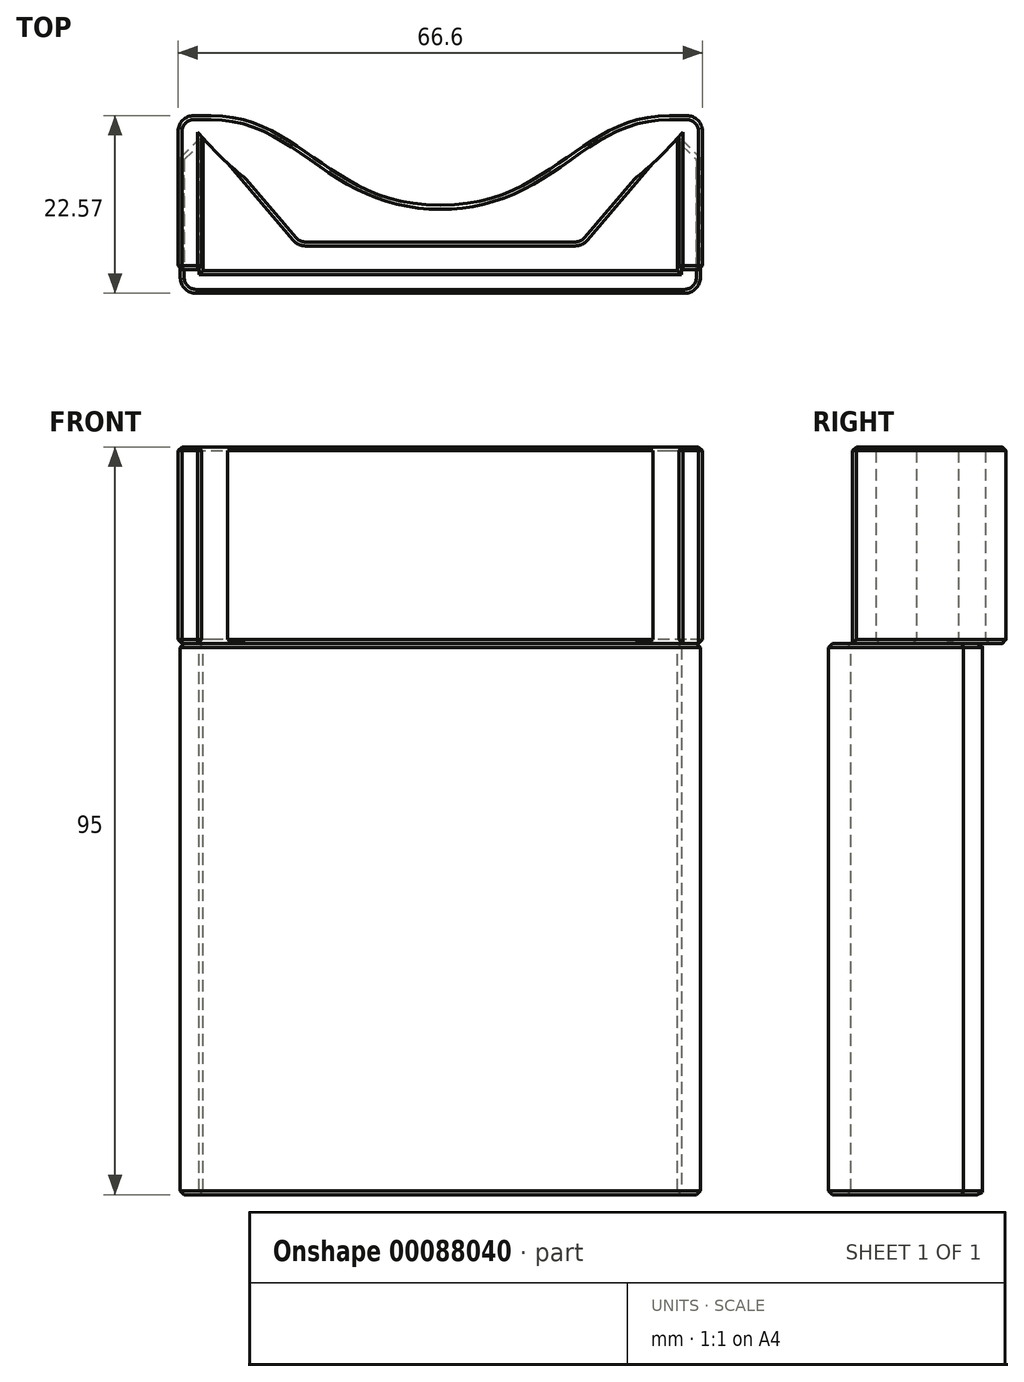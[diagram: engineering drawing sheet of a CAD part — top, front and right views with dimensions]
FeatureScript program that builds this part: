
annotation { "Feature Type Name" : "Feature", "Feature Type Description" : "" }
export const myFeature = defineFeature(function(context is Context, id is Id, definition is map)
    precondition{}
    {
        {
            var Q0;
            Q0=qCreatedBy(makeId("Top.planeOp"),FACE);
            var sketch = newSketch(context, id + "F0", { "sketchPlane" : qUnion([Q0])});
            skLineSegment(sketch, "E0", {"start": v(0, 0) * mm, "end": v(30, 0) * mm, "construction": true});
            skLineSegment(sketch, "E1", {"start": v(30, 0) * mm, "end": v(30, 40) * mm, "construction": true});
            skLineSegment(sketch, "E2", {"start": v(30, 40) * mm, "end": v(27, 40) * mm, "construction": true});
            skLineSegment(sketch, "E3", {"start": v(27, 40) * mm, "end": v(27, 3) * mm, "construction": true});
            skLineSegment(sketch, "E4", {"start": v(27, 3) * mm, "end": v(0, 3) * mm, "construction": true});
            skLineSegment(sketch, "E5", {"start": v(0, 3) * mm, "end": v(0, 0) * mm, "construction": true});
            skLineSegment(sketch, "E6.MirrorCS", {"start": v(-27, 3) * mm, "end": v(0, 3) * mm, "construction": true});
            skLineSegment(sketch, "E7.MirrorCS", {"start": v(0, 0) * mm, "end": v(-30, 0) * mm, "construction": true});
            skLineSegment(sketch, "E8.MirrorCS", {"start": v(-30, 0) * mm, "end": v(-30, 40) * mm, "construction": true});
            skLineSegment(sketch, "E9.MirrorCS", {"start": v(-27, 40) * mm, "end": v(-27, 3) * mm, "construction": true});
            skLineSegment(sketch, "E10.MirrorCS", {"start": v(-30, 40) * mm, "end": v(-27, 40) * mm, "construction": true});
            skArc(sketch, "E11", {"start": v(-30, 16.54) * mm, "mid": v(-28.54, 14.97) * mm, "end": v(-27, 13.49) * mm});
            skArc(sketch, "E12", {"start": v(-27, 13.49) * mm, "mid": v(0, 3) * mm, "end": v(27, 13.49) * mm, "construction": true});
            skArc(sketch, "E13", {"start": v(27, 13.49) * mm, "mid": v(28.54, 14.97) * mm, "end": v(30, 16.54) * mm});
            skArc(sketch, "E14", {"start": v(30, 16.54) * mm, "mid": v(0, 83) * mm, "end": v(-30, 16.54) * mm, "construction": true});
            skLineSegment(sketch, "E15", {"start": v(-27, 13.49) * mm, "end": v(-18.68, 3.7) * mm});
            skLineSegment(sketch, "E16", {"start": v(-17.15, 3) * mm, "end": v(0, 3) * mm});
            skLineSegment(sketch, "E17", {"start": v(-30.3, 16.54) * mm, "end": v(-30.3, 0) * mm});
            skLineSegment(sketch, "E18", {"start": v(-30.3, 0) * mm, "end": v(-33.3, 0) * mm});
            skLineSegment(sketch, "E19", {"start": v(-33.3, 0) * mm, "end": v(-33.3, 17.54) * mm});
            skLineSegment(sketch, "E20", {"start": v(-31.3, 19.54) * mm, "end": v(-29.14, 19.54) * mm});
            skLineSegment(sketch, "E21", {"start": v(0, 6) * mm, "end": v(0, 3) * mm, "construction": true});
            skLineSegment(sketch, "E22.MirrorCS", {"start": v(17.15, 3) * mm, "end": v(0, 3) * mm});
            skLineSegment(sketch, "E23.MirrorCS", {"start": v(27, 13.49) * mm, "end": v(18.68, 3.7) * mm});
            skLineSegment(sketch, "E24.MirrorCS", {"start": v(31.3, 19.54) * mm, "end": v(29.14, 19.54) * mm});
            skLineSegment(sketch, "E25.MirrorCS", {"start": v(30.3, 16.54) * mm, "end": v(30.3, 0) * mm});
            skLineSegment(sketch, "E26.MirrorCS", {"start": v(33.3, 0) * mm, "end": v(33.3, 17.54) * mm});
            skLineSegment(sketch, "E27.MirrorCS", {"start": v(30.3, 0) * mm, "end": v(33.3, 0) * mm});
            skPoint(sketch, "E28.visualSharp", {"position": v(-33.3, 19.54) * mm});
            skArc(sketch, "E28.filletArc", {"start": v(-31.3, 19.54) * mm, "mid": v(-32.71, 18.96) * mm, "end": v(-33.3, 17.54) * mm});
            skPoint(sketch, "E29.visualSharp", {"position": v(-16.7, 6) * mm});
            skPoint(sketch, "E30.visualSharp", {"position": v(-18.08, 3) * mm});
            skArc(sketch, "E30.filletArc", {"start": v(-18.68, 3.7) * mm, "mid": v(-18, 3.18) * mm, "end": v(-17.15, 3) * mm});
            skPoint(sketch, "E31.visualSharp", {"position": v(18.08, 3) * mm});
            skArc(sketch, "E31.filletArc", {"start": v(17.15, 3) * mm, "mid": v(18, 3.18) * mm, "end": v(18.68, 3.7) * mm});
            skPoint(sketch, "E32.visualSharp", {"position": v(16.7, 6) * mm});
            skArc(sketch, "E32.filletArc", {"start": v(15.77, 6) * mm, "mid": v(16.6, 6.18) * mm, "end": v(17.29, 6.7) * mm});
            skPoint(sketch, "E33.visualSharp", {"position": v(28.21, 19.54) * mm});
            skPoint(sketch, "E34.visualSharp", {"position": v(33.3, 19.54) * mm});
            skArc(sketch, "E34.filletArc", {"start": v(33.3, 17.54) * mm, "mid": v(32.71, 18.96) * mm, "end": v(31.3, 19.54) * mm});
            skLineSegment(sketch, "E35", {"start": v(-30.3, 16.54) * mm, "end": v(-30.3, 16.89) * mm});
            skLineSegment(sketch, "E36", {"start": v(-30.3, 16.89) * mm, "end": v(-30, 16.54) * mm});
            skLineSegment(sketch, "E37", {"start": v(30.3, 16.54) * mm, "end": v(30.3, 16.89) * mm});
            skLineSegment(sketch, "E38", {"start": v(30.3, 16.89) * mm, "end": v(30, 16.54) * mm});
            skFitSpline(sketch, "E39", {"points": [v(-29.14, 19.54) * mm, v(0, 8.16) * mm], "startDerivative": vector(34.38, 0) * mm, "endDerivative": vector(42.32, 0) * mm});
            skFitSpline(sketch, "E40.MirrorCS", {"points": [v(29.14, 19.54) * mm, v(0, 8.16) * mm], "startDerivative": vector(-34.38, 0) * mm, "endDerivative": vector(-42.32, 0) * mm});
            skSolve(sketch);
        }
        {
            var Q0;
            Q0 = qSketchRegion(id + "F0", true);
            extrude(context, id + "F1", {"entities" : qUnion([Q0]), "depth" : 25 * mm});
        }
        {
            var Q0;
            Q0=makeQuery(id+"F1.opExtrude","CAP_EDGE",EDGE,{"disambiguationData":[OSD([sQuery(id+"F0.wireOp",EDGE,"E23.MirrorCS")])],"isStart":true});
            var Q1;
            Q1=makeQuery(id+"F1.opExtrude","CAP_EDGE",EDGE,{"disambiguationData":[OSD([sQuery(id+"F0.wireOp",EDGE,"E25.MirrorCS"),sQuery(id+"F0.wireOp",EDGE,"E37")])],"isStart":true});
            var Q2;
            Q2=makeQuery(id+"F1.opExtrude","CAP_EDGE",EDGE,{"disambiguationData":[OSD([sQuery(id+"F0.wireOp",EDGE,"E26.MirrorCS")])],"isStart":true});
            var Q3;
            Q3=makeQuery(id+"F1.opExtrude","CAP_EDGE",EDGE,{"disambiguationData":[OSD([sQuery(id+"F0.wireOp",EDGE,"E26.MirrorCS")])],"isStart":false});
            var Q4;
            Q4=makeQuery(id+"F1.opExtrude","CAP_EDGE",EDGE,{"disambiguationData":[OSD([sQuery(id+"F0.wireOp",EDGE,"E16"),sQuery(id+"F0.wireOp",EDGE,"E22.MirrorCS")])],"isStart":false});
            var Q5;
            Q5=makeQuery(id+"F1.opExtrude","CAP_EDGE",EDGE,{"disambiguationData":[OSD([sQuery(id+"F0.wireOp",EDGE,"E25.MirrorCS"),sQuery(id+"F0.wireOp",EDGE,"E37")])],"isStart":false});
            var Q6;
            Q6=makeQuery(id+"F1.opExtrude","CAP_EDGE",EDGE,{"disambiguationData":[OSD([sQuery(id+"F0.wireOp",EDGE,"E27.MirrorCS")])],"isStart":false});
            var Q7;
            Q7=makeQuery(id+"F1.opExtrude","CAP_EDGE",EDGE,{"disambiguationData":[OSD([sQuery(id+"F0.wireOp",EDGE,"E18")])],"isStart":false});
            var Q8;
            Q8=makeQuery(id+"F1.opExtrude","CAP_EDGE",EDGE,{"disambiguationData":[OSD([sQuery(id+"F0.wireOp",EDGE,"E17"),sQuery(id+"F0.wireOp",EDGE,"E35")])],"isStart":false});
            var Q9;
            Q9=makeQuery(id+"F1.opExtrude","SWEPT_EDGE",EDGE,{"disambiguationData":[OSD([sQuery(id+"F0.wireOp",EDGE,"E18"),sQuery(id+"F0.wireOp",EDGE,"E19")])]});
            var Q10;
            Q10=makeQuery(id+"F1.opExtrude","SWEPT_EDGE",EDGE,{"disambiguationData":[OSD([sQuery(id+"F0.wireOp",EDGE,"E25.MirrorCS"),sQuery(id+"F0.wireOp",EDGE,"E27.MirrorCS")])]});
            var Q11;
            Q11=makeQuery(id+"F1.opExtrude","SWEPT_EDGE",EDGE,{"disambiguationData":[OSD([sQuery(id+"F0.wireOp",EDGE,"E26.MirrorCS"),sQuery(id+"F0.wireOp",EDGE,"E27.MirrorCS")])]});
            var Q12;
            Q12=makeQuery(id+"F1.opExtrude","SWEPT_EDGE",EDGE,{"disambiguationData":[OSD([sQuery(id+"F0.wireOp",EDGE,"E17"),sQuery(id+"F0.wireOp",EDGE,"E18")])]});
            var Q13;
            Q13=makeQuery(id+"F1.opExtrude","CAP_EDGE",EDGE,{"disambiguationData":[OSD([sQuery(id+"F0.wireOp",EDGE,"E18")])],"isStart":true});
            var Q14;
            Q14=makeQuery(id+"F1.opExtrude","CAP_EDGE",EDGE,{"disambiguationData":[OSD([sQuery(id+"F0.wireOp",EDGE,"E17"),sQuery(id+"F0.wireOp",EDGE,"E35")])],"isStart":true});
            chamfer(context, id + "F2", {"entities" : qUnion([Q0, Q1, Q2, Q3, Q4, Q5, Q6, Q7, Q8, Q9, Q10, Q11, Q12, Q13, Q14]), "width" : 0.5 * mm, "tangentPropagation" : true});
        }
        {
            var Q0;
            Q0=qCreatedBy(makeId("Top.planeOp"),FACE);
            var sketch = newSketch(context, id + "F3", { "sketchPlane" : qUnion([Q0])});
            skPoint(sketch, "E41.0", {"position": v(-30, 16.54) * mm});
            skLineSegment(sketch, "E41.1", {"start": v(0, 0) * mm, "end": v(-30, 0) * mm, "construction": true});
            skLineSegment(sketch, "E41.2", {"start": v(0, 3) * mm, "end": v(0, 0) * mm, "construction": true});
            skLineSegment(sketch, "E42", {"start": v(-30, 0) * mm, "end": v(-30, 16.54) * mm, "construction": true});
            skLineSegment(sketch, "E43", {"start": v(-30.15, 16.54) * mm, "end": v(-30.15, -0.15) * mm});
            skLineSegment(sketch, "E44", {"start": v(-30.15, -0.15) * mm, "end": v(0, -0.15) * mm});
            skLineSegment(sketch, "E45", {"start": v(-30.15, 16.54) * mm, "end": v(-33.03, 16.54) * mm});
            skLineSegment(sketch, "E46", {"start": v(-33.03, 16.54) * mm, "end": v(-33.03, -3.03) * mm});
            skLineSegment(sketch, "E47", {"start": v(-33.03, -3.03) * mm, "end": v(0, -3.03) * mm});
            skLineSegment(sketch, "E48.MirrorCS", {"start": v(30.15, -0.15) * mm, "end": v(0, -0.15) * mm});
            skLineSegment(sketch, "E49.MirrorCS", {"start": v(33.03, -3.03) * mm, "end": v(0, -3.03) * mm});
            skLineSegment(sketch, "E50.MirrorCS", {"start": v(30.15, 16.54) * mm, "end": v(30.15, -0.15) * mm});
            skLineSegment(sketch, "E51.MirrorCS", {"start": v(33.03, 16.54) * mm, "end": v(33.03, -3.03) * mm});
            skLineSegment(sketch, "E52.MirrorCS", {"start": v(30.15, 16.54) * mm, "end": v(33.03, 16.54) * mm});
            skLineSegment(sketch, "E53", {"start": v(-30.15, -0.15) * mm, "end": v(-30.15, -3.03) * mm, "construction": true});
            skSolve(sketch);
        }
        {
            var Q0;
            Q0=makeQuery(id+"F3.imprint","IMPRINT",FACE,{"disambiguationData":[TD([[makeQuery(id+"F3.imprint","IMPRINT",EDGE,{"derivedFrom":sQuery(id+"F3.wireOp",EDGE,"E43")}),-1.0]])]});
            extrude(context, id + "F4", {"entities" : qUnion([Q0]), "oppositeDirection" : true, "depth" : 70 * mm});
        }
        {
            var Q0;
            Q0=makeQuery(id+"F4.opExtrude","SWEPT_EDGE",EDGE,{"disambiguationData":[OSD([sQuery(id+"F3.wireOp",EDGE,"E45"),sQuery(id+"F3.wireOp",EDGE,"E46")])]});
            var Q1;
            Q1=makeQuery(id+"F4.opExtrude","SWEPT_EDGE",EDGE,{"disambiguationData":[OSD([sQuery(id+"F3.wireOp",EDGE,"E51.MirrorCS"),sQuery(id+"F3.wireOp",EDGE,"E52.MirrorCS")])]});
            chamfer(context, id + "F5", {"entities" : qUnion([Q0, Q1]), "width" : (5 * 0.48) * mm, "tangentPropagation" : true});
        }
        {
            var Q0;
            Q0=makeQuery(id+"F4.opExtrude","SWEPT_EDGE",EDGE,{"disambiguationData":[OSD([sQuery(id+"F3.wireOp",EDGE,"E46"),sQuery(id+"F3.wireOp",EDGE,"E47")])]});
            var Q1;
            Q1=makeQuery(id+"F4.opExtrude","SWEPT_EDGE",EDGE,{"disambiguationData":[OSD([sQuery(id+"F3.wireOp",EDGE,"E49.MirrorCS"),sQuery(id+"F3.wireOp",EDGE,"E51.MirrorCS")])]});
            fillet(context, id + "F6", {"entities" : qUnion([Q0, Q1]), "radius" : 2 * mm, "tangentPropagation" : true, "allowEdgeOverflow" : false});
        }
        {
            var Q0;
            Q0=makeQuery(id+"F4.opExtrude","CAP_EDGE",EDGE,{"disambiguationData":[OSD([sQuery(id+"F3.wireOp",EDGE,"E46")])],"isStart":true});
            var Q1;
            {var subQ0=sQuery(id+"F3.wireOp",EDGE,"E46");var subQ1=sQuery(id+"F3.wireOp",EDGE,"E45");Q1=makeQuery(id+"F5.opChamfer","BLEND_EDGE",EDGE,{"blendedFrom":[makeQuery(id+"F4.opExtrude","SWEPT_EDGE",EDGE,{"disambiguationData":[OSD([subQ1,subQ0])]}),makeQuery(id+"F4.opExtrude","CAP_FACE",FACE,{"disambiguationData":[OSD([sQuery(id+"F3.wireOp",EDGE,"E43"),sQuery(id+"F3.wireOp",EDGE,"E44"),subQ1,subQ0,sQuery(id+"F3.wireOp",EDGE,"E47"),sQuery(id+"F3.wireOp",EDGE,"E48.MirrorCS"),sQuery(id+"F3.wireOp",EDGE,"E49.MirrorCS"),sQuery(id+"F3.wireOp",EDGE,"E50.MirrorCS"),sQuery(id+"F3.wireOp",EDGE,"E51.MirrorCS"),sQuery(id+"F3.wireOp",EDGE,"E52.MirrorCS")])],"isStart":true})],"blendedInto":[makeQuery(id+"F4.opExtrude","CAP_FACE",FACE,{"disambiguationData":[OSD([sQuery(id+"F3.wireOp",EDGE,"E43"),sQuery(id+"F3.wireOp",EDGE,"E44"),subQ1,subQ0,sQuery(id+"F3.wireOp",EDGE,"E47"),sQuery(id+"F3.wireOp",EDGE,"E48.MirrorCS"),sQuery(id+"F3.wireOp",EDGE,"E49.MirrorCS"),sQuery(id+"F3.wireOp",EDGE,"E50.MirrorCS"),sQuery(id+"F3.wireOp",EDGE,"E51.MirrorCS"),sQuery(id+"F3.wireOp",EDGE,"E52.MirrorCS")])],"isStart":true})]});}
            var Q2;
            Q2=makeQuery(id+"F4.opExtrude","CAP_EDGE",EDGE,{"disambiguationData":[OSD([sQuery(id+"F3.wireOp",EDGE,"E43")])],"isStart":true});
            var Q3;
            Q3=makeQuery(id+"F4.opExtrude","CAP_EDGE",EDGE,{"disambiguationData":[OSD([sQuery(id+"F3.wireOp",EDGE,"E44"),sQuery(id+"F3.wireOp",EDGE,"E48.MirrorCS")])],"isStart":true});
            var Q4;
            Q4=makeQuery(id+"F4.opExtrude","CAP_EDGE",EDGE,{"disambiguationData":[OSD([sQuery(id+"F3.wireOp",EDGE,"E50.MirrorCS")])],"isStart":true});
            var Q5;
            {var subQ0=sQuery(id+"F3.wireOp",EDGE,"E52.MirrorCS");var subQ1=sQuery(id+"F3.wireOp",EDGE,"E51.MirrorCS");Q5=makeQuery(id+"F5.opChamfer","BLEND_EDGE",EDGE,{"blendedFrom":[makeQuery(id+"F4.opExtrude","SWEPT_EDGE",EDGE,{"disambiguationData":[OSD([subQ1,subQ0])]}),makeQuery(id+"F4.opExtrude","CAP_FACE",FACE,{"disambiguationData":[OSD([sQuery(id+"F3.wireOp",EDGE,"E43"),sQuery(id+"F3.wireOp",EDGE,"E44"),sQuery(id+"F3.wireOp",EDGE,"E45"),sQuery(id+"F3.wireOp",EDGE,"E46"),sQuery(id+"F3.wireOp",EDGE,"E47"),sQuery(id+"F3.wireOp",EDGE,"E48.MirrorCS"),sQuery(id+"F3.wireOp",EDGE,"E49.MirrorCS"),sQuery(id+"F3.wireOp",EDGE,"E50.MirrorCS"),subQ1,subQ0])],"isStart":true})],"blendedInto":[makeQuery(id+"F4.opExtrude","CAP_FACE",FACE,{"disambiguationData":[OSD([sQuery(id+"F3.wireOp",EDGE,"E43"),sQuery(id+"F3.wireOp",EDGE,"E44"),sQuery(id+"F3.wireOp",EDGE,"E45"),sQuery(id+"F3.wireOp",EDGE,"E46"),sQuery(id+"F3.wireOp",EDGE,"E47"),sQuery(id+"F3.wireOp",EDGE,"E48.MirrorCS"),sQuery(id+"F3.wireOp",EDGE,"E49.MirrorCS"),sQuery(id+"F3.wireOp",EDGE,"E50.MirrorCS"),subQ1,subQ0])],"isStart":true})]});}
            var Q6;
            Q6=makeQuery(id+"F4.opExtrude","CAP_EDGE",EDGE,{"disambiguationData":[OSD([sQuery(id+"F3.wireOp",EDGE,"E46")])],"isStart":false});
            var Q7;
            Q7=makeQuery(id+"F4.opExtrude","CAP_EDGE",EDGE,{"disambiguationData":[OSD([sQuery(id+"F3.wireOp",EDGE,"E43")])],"isStart":false});
            var Q8;
            Q8=makeQuery(id+"F4.opExtrude","CAP_EDGE",EDGE,{"disambiguationData":[OSD([sQuery(id+"F3.wireOp",EDGE,"E44"),sQuery(id+"F3.wireOp",EDGE,"E48.MirrorCS")])],"isStart":false});
            var Q9;
            Q9=makeQuery(id+"F4.opExtrude","CAP_EDGE",EDGE,{"disambiguationData":[OSD([sQuery(id+"F3.wireOp",EDGE,"E50.MirrorCS")])],"isStart":false});
            var Q10;
            {var subQ0=sQuery(id+"F3.wireOp",EDGE,"E52.MirrorCS");var subQ1=sQuery(id+"F3.wireOp",EDGE,"E51.MirrorCS");Q10=makeQuery(id+"F5.opChamfer","BLEND_EDGE",EDGE,{"blendedFrom":[makeQuery(id+"F4.opExtrude","SWEPT_EDGE",EDGE,{"disambiguationData":[OSD([subQ1,subQ0])]}),makeQuery(id+"F4.opExtrude","CAP_FACE",FACE,{"disambiguationData":[OSD([sQuery(id+"F3.wireOp",EDGE,"E43"),sQuery(id+"F3.wireOp",EDGE,"E44"),sQuery(id+"F3.wireOp",EDGE,"E45"),sQuery(id+"F3.wireOp",EDGE,"E46"),sQuery(id+"F3.wireOp",EDGE,"E47"),sQuery(id+"F3.wireOp",EDGE,"E48.MirrorCS"),sQuery(id+"F3.wireOp",EDGE,"E49.MirrorCS"),sQuery(id+"F3.wireOp",EDGE,"E50.MirrorCS"),subQ1,subQ0])],"isStart":false})],"blendedInto":[makeQuery(id+"F4.opExtrude","CAP_FACE",FACE,{"disambiguationData":[OSD([sQuery(id+"F3.wireOp",EDGE,"E43"),sQuery(id+"F3.wireOp",EDGE,"E44"),sQuery(id+"F3.wireOp",EDGE,"E45"),sQuery(id+"F3.wireOp",EDGE,"E46"),sQuery(id+"F3.wireOp",EDGE,"E47"),sQuery(id+"F3.wireOp",EDGE,"E48.MirrorCS"),sQuery(id+"F3.wireOp",EDGE,"E49.MirrorCS"),sQuery(id+"F3.wireOp",EDGE,"E50.MirrorCS"),subQ1,subQ0])],"isStart":false})]});}
            var Q11;
            {var subQ0=sQuery(id+"F3.wireOp",EDGE,"E46");var subQ1=sQuery(id+"F3.wireOp",EDGE,"E45");Q11=makeQuery(id+"F5.opChamfer","BLEND_EDGE",EDGE,{"blendedFrom":[makeQuery(id+"F4.opExtrude","SWEPT_EDGE",EDGE,{"disambiguationData":[OSD([subQ1,subQ0])]}),makeQuery(id+"F4.opExtrude","CAP_FACE",FACE,{"disambiguationData":[OSD([sQuery(id+"F3.wireOp",EDGE,"E43"),sQuery(id+"F3.wireOp",EDGE,"E44"),subQ1,subQ0,sQuery(id+"F3.wireOp",EDGE,"E47"),sQuery(id+"F3.wireOp",EDGE,"E48.MirrorCS"),sQuery(id+"F3.wireOp",EDGE,"E49.MirrorCS"),sQuery(id+"F3.wireOp",EDGE,"E50.MirrorCS"),sQuery(id+"F3.wireOp",EDGE,"E51.MirrorCS"),sQuery(id+"F3.wireOp",EDGE,"E52.MirrorCS")])],"isStart":false})],"blendedInto":[makeQuery(id+"F4.opExtrude","CAP_FACE",FACE,{"disambiguationData":[OSD([sQuery(id+"F3.wireOp",EDGE,"E43"),sQuery(id+"F3.wireOp",EDGE,"E44"),subQ1,subQ0,sQuery(id+"F3.wireOp",EDGE,"E47"),sQuery(id+"F3.wireOp",EDGE,"E48.MirrorCS"),sQuery(id+"F3.wireOp",EDGE,"E49.MirrorCS"),sQuery(id+"F3.wireOp",EDGE,"E50.MirrorCS"),sQuery(id+"F3.wireOp",EDGE,"E51.MirrorCS"),sQuery(id+"F3.wireOp",EDGE,"E52.MirrorCS")])],"isStart":false})]});}
            chamfer(context, id + "F7", {"entities" : qUnion([Q0, Q1, Q2, Q3, Q4, Q5, Q6, Q7, Q8, Q9, Q10, Q11]), "width" : 0.5 * mm, "tangentPropagation" : true});
        }
    });
